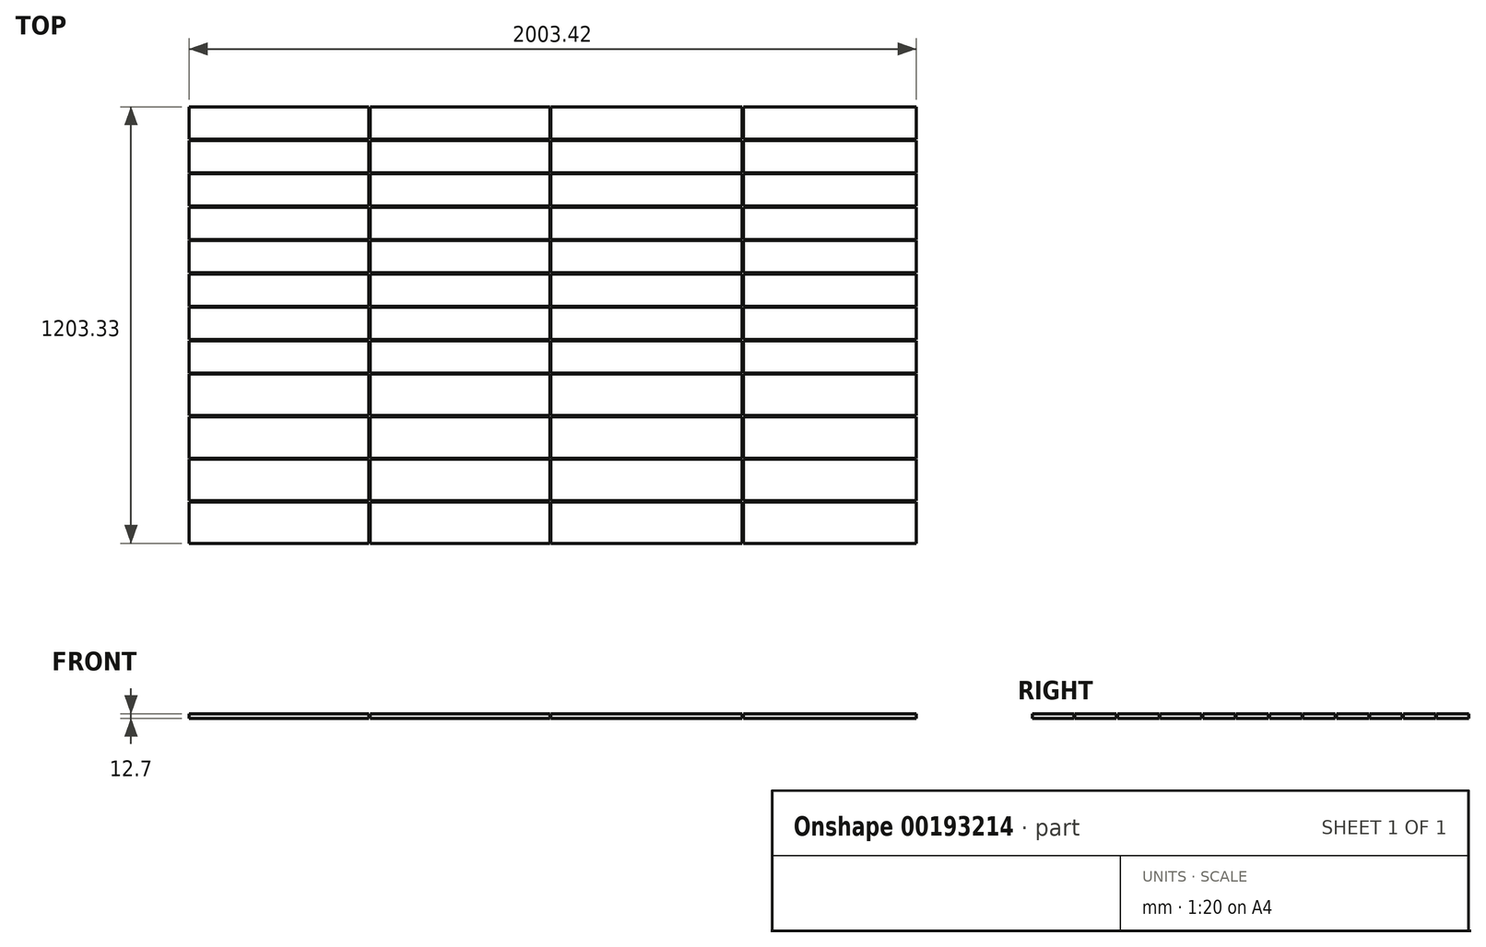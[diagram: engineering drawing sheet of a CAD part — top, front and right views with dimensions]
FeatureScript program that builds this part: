
annotation { "Feature Type Name" : "Feature", "Feature Type Description" : "" }
export const myFeature = defineFeature(function(context is Context, id is Id, definition is map)
    precondition{}
    {
        {
            var Q0;
            Q0=qCreatedBy(makeId("Top.planeOp"),FACE);
            var sketch = newSketch(context, id + "F0", { "sketchPlane" : qUnion([Q0])});
            skLineSegment(sketch, "E0.bottom", {"start": v(0, 0) * mm, "end": v(495.3, 0) * mm});
            skLineSegment(sketch, "E0.left", {"start": v(0, 0) * mm, "end": v(0, -88.9) * mm});
            skLineSegment(sketch, "E1.top", {"start": v(0, -88.9) * mm, "end": v(495.3, -88.9) * mm});
            skLineSegment(sketch, "E1.right", {"start": v(495.3, 0) * mm, "end": v(495.3, -88.9) * mm});
            skLineSegment(sketch, "E2.0.1.0", {"start": v(495.3, -92.07) * mm, "end": v(495.3, -180.97) * mm});
            skLineSegment(sketch, "E2.0.1.1", {"start": v(0, -180.98) * mm, "end": v(495.3, -180.98) * mm});
            skLineSegment(sketch, "E2.0.1.2", {"start": v(0, -92.08) * mm, "end": v(0, -180.98) * mm});
            skLineSegment(sketch, "E2.0.1.3", {"start": v(0, -92.08) * mm, "end": v(495.3, -92.08) * mm});
            skLineSegment(sketch, "E2.0.2.0", {"start": v(495.3, -184.15) * mm, "end": v(495.3, -273.05) * mm});
            skLineSegment(sketch, "E2.0.2.1", {"start": v(0, -273.05) * mm, "end": v(495.3, -273.05) * mm});
            skLineSegment(sketch, "E2.0.2.2", {"start": v(0, -184.15) * mm, "end": v(0, -273.05) * mm});
            skLineSegment(sketch, "E2.0.2.3", {"start": v(0, -184.15) * mm, "end": v(495.3, -184.15) * mm});
            skLineSegment(sketch, "E2.0.3.0", {"start": v(495.3, -276.22) * mm, "end": v(495.3, -365.12) * mm});
            skLineSegment(sketch, "E2.0.3.1", {"start": v(0, -365.13) * mm, "end": v(495.3, -365.13) * mm});
            skLineSegment(sketch, "E2.0.3.2", {"start": v(0, -276.23) * mm, "end": v(0, -365.13) * mm});
            skLineSegment(sketch, "E2.0.3.3", {"start": v(0, -276.23) * mm, "end": v(495.3, -276.23) * mm});
            skLineSegment(sketch, "E2.0.4.0", {"start": v(495.3, -368.3) * mm, "end": v(495.3, -457.2) * mm});
            skLineSegment(sketch, "E2.0.4.1", {"start": v(0, -457.2) * mm, "end": v(495.3, -457.2) * mm});
            skLineSegment(sketch, "E2.0.4.2", {"start": v(0, -368.3) * mm, "end": v(0, -457.2) * mm});
            skLineSegment(sketch, "E2.0.4.3", {"start": v(0, -368.3) * mm, "end": v(495.3, -368.3) * mm});
            skLineSegment(sketch, "E2.0.5.0", {"start": v(495.3, -460.37) * mm, "end": v(495.3, -549.27) * mm});
            skLineSegment(sketch, "E2.0.5.1", {"start": v(0, -549.28) * mm, "end": v(495.3, -549.28) * mm});
            skLineSegment(sketch, "E2.0.5.2", {"start": v(0, -460.38) * mm, "end": v(0, -549.27) * mm});
            skLineSegment(sketch, "E2.0.5.3", {"start": v(0, -460.38) * mm, "end": v(495.3, -460.38) * mm});
            skLineSegment(sketch, "E2.0.6.0", {"start": v(495.3, -552.45) * mm, "end": v(495.3, -641.35) * mm});
            skLineSegment(sketch, "E2.0.6.1", {"start": v(0, -641.35) * mm, "end": v(495.3, -641.35) * mm});
            skLineSegment(sketch, "E2.0.6.2", {"start": v(0, -552.45) * mm, "end": v(0, -641.35) * mm});
            skLineSegment(sketch, "E2.0.6.3", {"start": v(0, -552.45) * mm, "end": v(495.3, -552.45) * mm});
            skLineSegment(sketch, "E2.0.7.0", {"start": v(495.3, -644.52) * mm, "end": v(495.3, -733.42) * mm});
            skLineSegment(sketch, "E2.0.7.1", {"start": v(0, -733.42) * mm, "end": v(495.3, -733.42) * mm});
            skLineSegment(sketch, "E2.0.7.2", {"start": v(0, -644.52) * mm, "end": v(0, -733.42) * mm});
            skLineSegment(sketch, "E2.0.7.3", {"start": v(0, -644.52) * mm, "end": v(495.3, -644.52) * mm});
            skLineSegment(sketch, "E2.1.0.0", {"start": v(993.78, 0) * mm, "end": v(993.78, -88.9) * mm});
            skLineSegment(sketch, "E2.1.0.1", {"start": v(498.48, -88.9) * mm, "end": v(993.78, -88.9) * mm});
            skLineSegment(sketch, "E2.1.0.2", {"start": v(498.48, 0) * mm, "end": v(498.48, -88.9) * mm});
            skLineSegment(sketch, "E2.1.0.3", {"start": v(498.48, 0) * mm, "end": v(993.78, 0) * mm});
            skLineSegment(sketch, "E2.1.1.0", {"start": v(993.78, -92.07) * mm, "end": v(993.78, -180.97) * mm});
            skLineSegment(sketch, "E2.1.1.1", {"start": v(498.48, -180.98) * mm, "end": v(993.78, -180.98) * mm});
            skLineSegment(sketch, "E2.1.1.2", {"start": v(498.48, -92.08) * mm, "end": v(498.48, -180.97) * mm});
            skLineSegment(sketch, "E2.1.1.3", {"start": v(498.48, -92.08) * mm, "end": v(993.78, -92.08) * mm});
            skLineSegment(sketch, "E2.1.2.0", {"start": v(993.78, -184.15) * mm, "end": v(993.78, -273.05) * mm});
            skLineSegment(sketch, "E2.1.2.1", {"start": v(498.48, -273.05) * mm, "end": v(993.78, -273.05) * mm});
            skLineSegment(sketch, "E2.1.2.2", {"start": v(498.48, -184.15) * mm, "end": v(498.48, -273.05) * mm});
            skLineSegment(sketch, "E2.1.2.3", {"start": v(498.48, -184.15) * mm, "end": v(993.78, -184.15) * mm});
            skLineSegment(sketch, "E2.1.3.0", {"start": v(993.78, -276.22) * mm, "end": v(993.78, -365.12) * mm});
            skLineSegment(sketch, "E2.1.3.1", {"start": v(498.48, -365.13) * mm, "end": v(993.78, -365.13) * mm});
            skLineSegment(sketch, "E2.1.3.2", {"start": v(498.48, -276.23) * mm, "end": v(498.48, -365.13) * mm});
            skLineSegment(sketch, "E2.1.3.3", {"start": v(498.48, -276.23) * mm, "end": v(993.78, -276.23) * mm});
            skLineSegment(sketch, "E2.1.4.0", {"start": v(993.78, -368.3) * mm, "end": v(993.78, -457.2) * mm});
            skLineSegment(sketch, "E2.1.4.1", {"start": v(498.48, -457.2) * mm, "end": v(993.78, -457.2) * mm});
            skLineSegment(sketch, "E2.1.4.2", {"start": v(498.48, -368.3) * mm, "end": v(498.48, -457.2) * mm});
            skLineSegment(sketch, "E2.1.4.3", {"start": v(498.48, -368.3) * mm, "end": v(993.78, -368.3) * mm});
            skLineSegment(sketch, "E2.1.5.0", {"start": v(993.78, -460.37) * mm, "end": v(993.78, -549.27) * mm});
            skLineSegment(sketch, "E2.1.5.1", {"start": v(498.48, -549.28) * mm, "end": v(993.78, -549.28) * mm});
            skLineSegment(sketch, "E2.1.5.2", {"start": v(498.48, -460.38) * mm, "end": v(498.48, -549.28) * mm});
            skLineSegment(sketch, "E2.1.5.3", {"start": v(498.48, -460.38) * mm, "end": v(993.78, -460.38) * mm});
            skLineSegment(sketch, "E2.1.6.0", {"start": v(993.78, -552.45) * mm, "end": v(993.78, -641.35) * mm});
            skLineSegment(sketch, "E2.1.6.1", {"start": v(498.48, -641.35) * mm, "end": v(993.78, -641.35) * mm});
            skLineSegment(sketch, "E2.1.6.2", {"start": v(498.48, -552.45) * mm, "end": v(498.48, -641.35) * mm});
            skLineSegment(sketch, "E2.1.6.3", {"start": v(498.48, -552.45) * mm, "end": v(993.78, -552.45) * mm});
            skLineSegment(sketch, "E2.1.7.0", {"start": v(993.78, -644.52) * mm, "end": v(993.78, -733.42) * mm});
            skLineSegment(sketch, "E2.1.7.1", {"start": v(498.48, -733.42) * mm, "end": v(993.78, -733.42) * mm});
            skLineSegment(sketch, "E2.1.7.2", {"start": v(498.48, -644.52) * mm, "end": v(498.48, -733.42) * mm});
            skLineSegment(sketch, "E2.1.7.3", {"start": v(498.48, -644.52) * mm, "end": v(993.78, -644.52) * mm});
            skLineSegment(sketch, "E2.direction1", {"start": v(495.3, -88.9) * mm, "end": v(993.78, -88.9) * mm, "construction": true});
            skLineSegment(sketch, "E2.direction2", {"start": v(495.3, -88.9) * mm, "end": v(495.3, -180.97) * mm, "construction": true});
            skLineSegment(sketch, "E3.bottom", {"start": v(996.95, 0) * mm, "end": v(1524, 0) * mm});
            skLineSegment(sketch, "E3.top", {"start": v(996.95, -88.9) * mm, "end": v(1524, -88.9) * mm});
            skLineSegment(sketch, "E3.left", {"start": v(996.95, 0) * mm, "end": v(996.95, -88.9) * mm});
            skLineSegment(sketch, "E3.right", {"start": v(1524, 0) * mm, "end": v(1524, -88.9) * mm});
            skLineSegment(sketch, "E4.0.1.0", {"start": v(1524, -92.08) * mm, "end": v(1524, -180.98) * mm});
            skLineSegment(sketch, "E4.0.1.1", {"start": v(996.95, -180.98) * mm, "end": v(1524, -180.98) * mm});
            skLineSegment(sketch, "E4.0.1.2", {"start": v(996.95, -92.08) * mm, "end": v(996.95, -180.97) * mm});
            skLineSegment(sketch, "E4.0.1.3", {"start": v(996.95, -92.08) * mm, "end": v(1524, -92.08) * mm});
            skLineSegment(sketch, "E4.0.2.0", {"start": v(1524, -184.15) * mm, "end": v(1524, -273.05) * mm});
            skLineSegment(sketch, "E4.0.2.1", {"start": v(996.95, -273.05) * mm, "end": v(1524, -273.05) * mm});
            skLineSegment(sketch, "E4.0.2.2", {"start": v(996.95, -184.15) * mm, "end": v(996.95, -273.05) * mm});
            skLineSegment(sketch, "E4.0.2.3", {"start": v(996.95, -184.15) * mm, "end": v(1524, -184.15) * mm});
            skLineSegment(sketch, "E4.0.3.0", {"start": v(1524, -276.23) * mm, "end": v(1524, -365.13) * mm});
            skLineSegment(sketch, "E4.0.3.1", {"start": v(996.95, -365.13) * mm, "end": v(1524, -365.13) * mm});
            skLineSegment(sketch, "E4.0.3.2", {"start": v(996.95, -276.23) * mm, "end": v(996.95, -365.13) * mm});
            skLineSegment(sketch, "E4.0.3.3", {"start": v(996.95, -276.23) * mm, "end": v(1524, -276.23) * mm});
            skLineSegment(sketch, "E4.0.4.0", {"start": v(1524, -368.3) * mm, "end": v(1524, -457.2) * mm});
            skLineSegment(sketch, "E4.0.4.1", {"start": v(996.95, -457.2) * mm, "end": v(1524, -457.2) * mm});
            skLineSegment(sketch, "E4.0.4.2", {"start": v(996.95, -368.3) * mm, "end": v(996.95, -457.2) * mm});
            skLineSegment(sketch, "E4.0.4.3", {"start": v(996.95, -368.3) * mm, "end": v(1524, -368.3) * mm});
            skLineSegment(sketch, "E4.0.5.0", {"start": v(1524, -460.38) * mm, "end": v(1524, -549.28) * mm});
            skLineSegment(sketch, "E4.0.5.1", {"start": v(996.95, -549.28) * mm, "end": v(1524, -549.28) * mm});
            skLineSegment(sketch, "E4.0.5.2", {"start": v(996.95, -460.38) * mm, "end": v(996.95, -549.28) * mm});
            skLineSegment(sketch, "E4.0.5.3", {"start": v(996.95, -460.38) * mm, "end": v(1524, -460.38) * mm});
            skLineSegment(sketch, "E4.0.6.0", {"start": v(1524, -552.45) * mm, "end": v(1524, -641.35) * mm});
            skLineSegment(sketch, "E4.0.6.1", {"start": v(996.95, -641.35) * mm, "end": v(1524, -641.35) * mm});
            skLineSegment(sketch, "E4.0.6.2", {"start": v(996.95, -552.45) * mm, "end": v(996.95, -641.35) * mm});
            skLineSegment(sketch, "E4.0.6.3", {"start": v(996.95, -552.45) * mm, "end": v(1524, -552.45) * mm});
            skLineSegment(sketch, "E4.0.7.0", {"start": v(1524, -644.52) * mm, "end": v(1524, -733.42) * mm});
            skLineSegment(sketch, "E4.0.7.1", {"start": v(996.95, -733.43) * mm, "end": v(1524, -733.43) * mm});
            skLineSegment(sketch, "E4.0.7.2", {"start": v(996.95, -644.52) * mm, "end": v(996.95, -733.42) * mm});
            skLineSegment(sketch, "E4.0.7.3", {"start": v(996.95, -644.53) * mm, "end": v(1524, -644.53) * mm});
            skLineSegment(sketch, "E4.direction1", {"start": v(1511.3, -88.9) * mm, "end": v(1524, -88.9) * mm, "construction": true});
            skLineSegment(sketch, "E4.direction2", {"start": v(1524, -88.9) * mm, "end": v(1524, -180.98) * mm, "construction": true});
            skLineSegment(sketch, "E5.bottom", {"start": v(1527.17, 0) * mm, "end": v(2003.42, 0) * mm});
            skLineSegment(sketch, "E5.top", {"start": v(1527.17, -88.9) * mm, "end": v(2003.42, -88.9) * mm});
            skLineSegment(sketch, "E5.left", {"start": v(1527.17, 0) * mm, "end": v(1527.17, -88.9) * mm});
            skLineSegment(sketch, "E5.right", {"start": v(2003.42, 0) * mm, "end": v(2003.42, -88.9) * mm});
            skLineSegment(sketch, "E6.0.1.0", {"start": v(2003.42, -92.07) * mm, "end": v(2003.42, -180.97) * mm});
            skLineSegment(sketch, "E6.0.1.1", {"start": v(1527.17, -180.98) * mm, "end": v(2003.42, -180.98) * mm});
            skLineSegment(sketch, "E6.0.1.2", {"start": v(1527.17, -92.08) * mm, "end": v(1527.17, -180.98) * mm});
            skLineSegment(sketch, "E6.0.1.3", {"start": v(1527.17, -92.08) * mm, "end": v(2003.42, -92.08) * mm});
            skLineSegment(sketch, "E6.0.2.0", {"start": v(2003.42, -184.15) * mm, "end": v(2003.42, -273.05) * mm});
            skLineSegment(sketch, "E6.0.2.1", {"start": v(1527.17, -273.05) * mm, "end": v(2003.42, -273.05) * mm});
            skLineSegment(sketch, "E6.0.2.2", {"start": v(1527.17, -184.15) * mm, "end": v(1527.17, -273.05) * mm});
            skLineSegment(sketch, "E6.0.2.3", {"start": v(1527.17, -184.15) * mm, "end": v(2003.42, -184.15) * mm});
            skLineSegment(sketch, "E6.0.3.0", {"start": v(2003.42, -276.22) * mm, "end": v(2003.42, -365.12) * mm});
            skLineSegment(sketch, "E6.0.3.1", {"start": v(1527.17, -365.13) * mm, "end": v(2003.42, -365.13) * mm});
            skLineSegment(sketch, "E6.0.3.2", {"start": v(1527.17, -276.23) * mm, "end": v(1527.17, -365.13) * mm});
            skLineSegment(sketch, "E6.0.3.3", {"start": v(1527.17, -276.23) * mm, "end": v(2003.42, -276.23) * mm});
            skLineSegment(sketch, "E6.0.4.0", {"start": v(2003.42, -368.3) * mm, "end": v(2003.42, -457.2) * mm});
            skLineSegment(sketch, "E6.0.4.1", {"start": v(1527.17, -457.2) * mm, "end": v(2003.42, -457.2) * mm});
            skLineSegment(sketch, "E6.0.4.2", {"start": v(1527.17, -368.3) * mm, "end": v(1527.17, -457.2) * mm});
            skLineSegment(sketch, "E6.0.4.3", {"start": v(1527.17, -368.3) * mm, "end": v(2003.42, -368.3) * mm});
            skLineSegment(sketch, "E6.0.5.0", {"start": v(2003.42, -460.38) * mm, "end": v(2003.42, -549.27) * mm});
            skLineSegment(sketch, "E6.0.5.1", {"start": v(1527.17, -549.28) * mm, "end": v(2003.42, -549.28) * mm});
            skLineSegment(sketch, "E6.0.5.2", {"start": v(1527.17, -460.38) * mm, "end": v(1527.17, -549.28) * mm});
            skLineSegment(sketch, "E6.0.5.3", {"start": v(1527.17, -460.38) * mm, "end": v(2003.42, -460.38) * mm});
            skLineSegment(sketch, "E6.0.6.0", {"start": v(2003.42, -552.45) * mm, "end": v(2003.42, -641.35) * mm});
            skLineSegment(sketch, "E6.0.6.1", {"start": v(1527.17, -641.35) * mm, "end": v(2003.42, -641.35) * mm});
            skLineSegment(sketch, "E6.0.6.2", {"start": v(1527.17, -552.45) * mm, "end": v(1527.17, -641.35) * mm});
            skLineSegment(sketch, "E6.0.6.3", {"start": v(1527.17, -552.45) * mm, "end": v(2003.42, -552.45) * mm});
            skLineSegment(sketch, "E6.0.7.0", {"start": v(2003.42, -644.52) * mm, "end": v(2003.42, -733.42) * mm});
            skLineSegment(sketch, "E6.0.7.1", {"start": v(1527.17, -733.43) * mm, "end": v(2003.42, -733.43) * mm});
            skLineSegment(sketch, "E6.0.7.2", {"start": v(1527.17, -644.52) * mm, "end": v(1527.17, -733.42) * mm});
            skLineSegment(sketch, "E6.0.7.3", {"start": v(1527.17, -644.53) * mm, "end": v(2003.42, -644.53) * mm});
            skLineSegment(sketch, "E6.direction1", {"start": v(2003.42, -88.9) * mm, "end": v(2009.77, -88.9) * mm, "construction": true});
            skLineSegment(sketch, "E6.direction2", {"start": v(2003.42, -88.9) * mm, "end": v(2003.42, -180.97) * mm, "construction": true});
            skLineSegment(sketch, "E7.bottom", {"start": v(0, -736.6) * mm, "end": v(495.3, -736.6) * mm});
            skLineSegment(sketch, "E7.top", {"start": v(0, -850.9) * mm, "end": v(495.3, -850.9) * mm});
            skLineSegment(sketch, "E7.left", {"start": v(0, -736.6) * mm, "end": v(0, -850.9) * mm});
            skLineSegment(sketch, "E7.right", {"start": v(495.3, -736.6) * mm, "end": v(495.3, -850.9) * mm});
            skLineSegment(sketch, "E8.0.1.0", {"start": v(495.3, -854.07) * mm, "end": v(495.3, -968.37) * mm});
            skLineSegment(sketch, "E8.0.1.1", {"start": v(0, -968.37) * mm, "end": v(495.3, -968.37) * mm});
            skLineSegment(sketch, "E8.0.1.2", {"start": v(0, -854.07) * mm, "end": v(495.3, -854.07) * mm});
            skLineSegment(sketch, "E8.0.1.3", {"start": v(0, -854.07) * mm, "end": v(0, -968.37) * mm});
            skLineSegment(sketch, "E8.0.2.0", {"start": v(495.3, -971.55) * mm, "end": v(495.3, -1085.85) * mm});
            skLineSegment(sketch, "E8.0.2.1", {"start": v(0, -1085.85) * mm, "end": v(495.3, -1085.85) * mm});
            skLineSegment(sketch, "E8.0.2.2", {"start": v(0, -971.55) * mm, "end": v(495.3, -971.55) * mm});
            skLineSegment(sketch, "E8.0.2.3", {"start": v(0, -971.55) * mm, "end": v(0, -1085.85) * mm});
            skLineSegment(sketch, "E8.0.3.0", {"start": v(495.3, -1089.02) * mm, "end": v(495.3, -1203.32) * mm});
            skLineSegment(sketch, "E8.0.3.1", {"start": v(0, -1203.32) * mm, "end": v(495.3, -1203.32) * mm});
            skLineSegment(sketch, "E8.0.3.2", {"start": v(0, -1089.02) * mm, "end": v(495.3, -1089.02) * mm});
            skLineSegment(sketch, "E8.0.3.3", {"start": v(0, -1089.02) * mm, "end": v(0, -1203.32) * mm});
            skLineSegment(sketch, "E8.1.0.0", {"start": v(993.78, -736.6) * mm, "end": v(993.78, -850.9) * mm});
            skLineSegment(sketch, "E8.1.0.1", {"start": v(498.48, -850.9) * mm, "end": v(993.78, -850.9) * mm});
            skLineSegment(sketch, "E8.1.0.2", {"start": v(498.48, -736.6) * mm, "end": v(993.78, -736.6) * mm});
            skLineSegment(sketch, "E8.1.0.3", {"start": v(498.48, -736.6) * mm, "end": v(498.48, -850.9) * mm});
            skLineSegment(sketch, "E8.1.1.0", {"start": v(993.78, -854.07) * mm, "end": v(993.78, -968.37) * mm});
            skLineSegment(sketch, "E8.1.1.1", {"start": v(498.48, -968.37) * mm, "end": v(993.78, -968.37) * mm});
            skLineSegment(sketch, "E8.1.1.2", {"start": v(498.48, -854.07) * mm, "end": v(993.78, -854.07) * mm});
            skLineSegment(sketch, "E8.1.1.3", {"start": v(498.48, -854.07) * mm, "end": v(498.48, -968.37) * mm});
            skLineSegment(sketch, "E8.1.2.0", {"start": v(993.78, -971.55) * mm, "end": v(993.78, -1085.85) * mm});
            skLineSegment(sketch, "E8.1.2.1", {"start": v(498.48, -1085.85) * mm, "end": v(993.78, -1085.85) * mm});
            skLineSegment(sketch, "E8.1.2.2", {"start": v(498.48, -971.55) * mm, "end": v(993.78, -971.55) * mm});
            skLineSegment(sketch, "E8.1.2.3", {"start": v(498.48, -971.55) * mm, "end": v(498.48, -1085.85) * mm});
            skLineSegment(sketch, "E8.1.3.0", {"start": v(993.78, -1089.02) * mm, "end": v(993.78, -1203.32) * mm});
            skLineSegment(sketch, "E8.1.3.1", {"start": v(498.48, -1203.32) * mm, "end": v(993.78, -1203.32) * mm});
            skLineSegment(sketch, "E8.1.3.2", {"start": v(498.48, -1089.02) * mm, "end": v(993.78, -1089.02) * mm});
            skLineSegment(sketch, "E8.1.3.3", {"start": v(498.48, -1089.02) * mm, "end": v(498.48, -1203.32) * mm});
            skLineSegment(sketch, "E8.direction1", {"start": v(495.3, -850.9) * mm, "end": v(993.78, -850.9) * mm, "construction": true});
            skLineSegment(sketch, "E8.direction2", {"start": v(495.3, -850.9) * mm, "end": v(495.3, -968.37) * mm, "construction": true});
            skLineSegment(sketch, "E9.bottom", {"start": v(996.95, -736.6) * mm, "end": v(1524, -736.6) * mm});
            skLineSegment(sketch, "E9.top", {"start": v(996.95, -850.9) * mm, "end": v(1524, -850.9) * mm});
            skLineSegment(sketch, "E9.left", {"start": v(996.95, -736.6) * mm, "end": v(996.95, -850.9) * mm});
            skLineSegment(sketch, "E9.right", {"start": v(1524, -736.6) * mm, "end": v(1524, -850.9) * mm});
            skLineSegment(sketch, "E10.0.1.0", {"start": v(1524, -854.08) * mm, "end": v(1524, -968.38) * mm});
            skLineSegment(sketch, "E10.0.1.1", {"start": v(996.95, -968.38) * mm, "end": v(1524, -968.38) * mm});
            skLineSegment(sketch, "E10.0.1.2", {"start": v(996.95, -854.08) * mm, "end": v(996.95, -968.38) * mm});
            skLineSegment(sketch, "E10.0.1.3", {"start": v(996.95, -854.08) * mm, "end": v(1524, -854.08) * mm});
            skLineSegment(sketch, "E10.0.2.0", {"start": v(1524, -971.55) * mm, "end": v(1524, -1085.85) * mm});
            skLineSegment(sketch, "E10.0.2.1", {"start": v(996.95, -1085.85) * mm, "end": v(1524, -1085.85) * mm});
            skLineSegment(sketch, "E10.0.2.2", {"start": v(996.95, -971.55) * mm, "end": v(996.95, -1085.85) * mm});
            skLineSegment(sketch, "E10.0.2.3", {"start": v(996.95, -971.55) * mm, "end": v(1524, -971.55) * mm});
            skLineSegment(sketch, "E10.0.3.0", {"start": v(1524, -1089.02) * mm, "end": v(1524, -1203.33) * mm});
            skLineSegment(sketch, "E10.0.3.1", {"start": v(996.95, -1203.33) * mm, "end": v(1524, -1203.33) * mm});
            skLineSegment(sketch, "E10.0.3.2", {"start": v(996.95, -1089.03) * mm, "end": v(996.95, -1203.33) * mm});
            skLineSegment(sketch, "E10.0.3.3", {"start": v(996.95, -1089.03) * mm, "end": v(1524, -1089.03) * mm});
            skLineSegment(sketch, "E10.direction1", {"start": v(1524, -850.9) * mm, "end": v(1549.4, -850.9) * mm, "construction": true});
            skLineSegment(sketch, "E10.direction2", {"start": v(1524, -850.9) * mm, "end": v(1524, -968.38) * mm, "construction": true});
            skLineSegment(sketch, "E11.bottom", {"start": v(1527.17, -736.6) * mm, "end": v(2003.42, -736.6) * mm});
            skLineSegment(sketch, "E11.top", {"start": v(1527.17, -850.9) * mm, "end": v(2003.42, -850.9) * mm});
            skLineSegment(sketch, "E11.left", {"start": v(1527.17, -736.6) * mm, "end": v(1527.17, -850.9) * mm});
            skLineSegment(sketch, "E11.right", {"start": v(2003.42, -736.6) * mm, "end": v(2003.42, -850.9) * mm});
            skLineSegment(sketch, "E12.0.1.0", {"start": v(2003.42, -854.07) * mm, "end": v(2003.42, -968.37) * mm});
            skLineSegment(sketch, "E12.0.1.1", {"start": v(1527.17, -968.38) * mm, "end": v(2003.42, -968.37) * mm});
            skLineSegment(sketch, "E12.0.1.2", {"start": v(1527.17, -854.08) * mm, "end": v(1527.17, -968.38) * mm});
            skLineSegment(sketch, "E12.0.1.3", {"start": v(1527.17, -854.08) * mm, "end": v(2003.42, -854.07) * mm});
            skLineSegment(sketch, "E12.0.2.0", {"start": v(2003.42, -971.55) * mm, "end": v(2003.42, -1085.85) * mm});
            skLineSegment(sketch, "E12.0.2.1", {"start": v(1527.17, -1085.85) * mm, "end": v(2003.42, -1085.85) * mm});
            skLineSegment(sketch, "E12.0.2.2", {"start": v(1527.17, -971.55) * mm, "end": v(1527.17, -1085.85) * mm});
            skLineSegment(sketch, "E12.0.2.3", {"start": v(1527.17, -971.55) * mm, "end": v(2003.42, -971.55) * mm});
            skLineSegment(sketch, "E12.0.3.0", {"start": v(2003.42, -1089.02) * mm, "end": v(2003.42, -1203.32) * mm});
            skLineSegment(sketch, "E12.0.3.1", {"start": v(1527.17, -1203.33) * mm, "end": v(2003.42, -1203.33) * mm});
            skLineSegment(sketch, "E12.0.3.2", {"start": v(1527.17, -1089.02) * mm, "end": v(1527.17, -1203.33) * mm});
            skLineSegment(sketch, "E12.0.3.3", {"start": v(1527.17, -1089.02) * mm, "end": v(2003.42, -1089.02) * mm});
            skLineSegment(sketch, "E12.direction1", {"start": v(2003.42, -850.9) * mm, "end": v(2028.82, -850.9) * mm, "construction": true});
            skLineSegment(sketch, "E12.direction2", {"start": v(2003.42, -850.9) * mm, "end": v(2003.42, -968.37) * mm, "construction": true});
            skLineSegment(sketch, "E13.trimOffspring", {"start": v(0, -460.38) * mm, "end": v(0, -549.28) * mm});
            skSolve(sketch);
        }
        {
            var Q0;
            Q0 = qSketchRegion(id + "F0", true);
            extrude(context, id + "F1", {"entities" : qUnion([Q0]), "depth" : 12.7 * mm});
        }
    });
